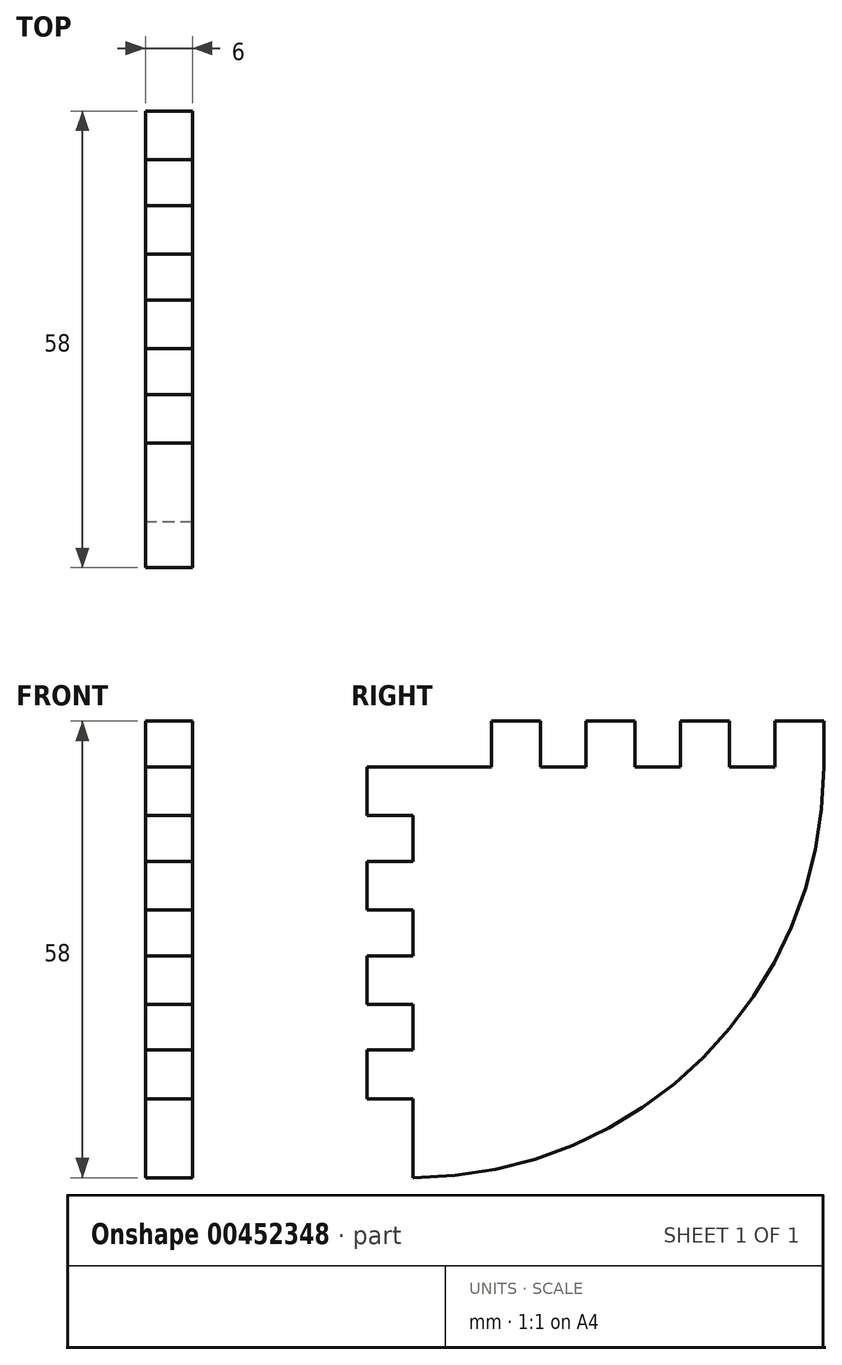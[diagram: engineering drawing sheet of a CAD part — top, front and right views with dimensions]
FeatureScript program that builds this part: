
annotation { "Feature Type Name" : "Feature", "Feature Type Description" : "" }
export const myFeature = defineFeature(function(context is Context, id is Id, definition is map)
    precondition{}
    {
        {
            var Q0;
            Q0=qCreatedBy(makeId("Right.planeOp"),FACE);
            var sketch = newSketch(context, id + "F0", { "sketchPlane" : qUnion([Q0])});
            skLineSegment(sketch, "E0", {"start": v(5.8, -52.2) * mm, "end": v(5.8, -42.2) * mm});
            skLineSegment(sketch, "E1", {"start": v(5.8, -42.2) * mm, "end": v(0, -42.2) * mm});
            skLineSegment(sketch, "E2", {"start": v(0, -42.2) * mm, "end": v(0, -36) * mm});
            skLineSegment(sketch, "E3", {"start": v(0, -36) * mm, "end": v(5.8, -36) * mm});
            skLineSegment(sketch, "E4", {"start": v(5.8, -36) * mm, "end": v(5.8, -30.2) * mm});
            skLineSegment(sketch, "E5", {"start": v(5.8, -30.2) * mm, "end": v(0, -30.2) * mm});
            skLineSegment(sketch, "E6", {"start": v(0, -30.2) * mm, "end": v(0, -24) * mm});
            skLineSegment(sketch, "E7", {"start": v(0, -24) * mm, "end": v(5.8, -24) * mm});
            skLineSegment(sketch, "E8", {"start": v(5.8, -24) * mm, "end": v(5.8, -18.2) * mm});
            skLineSegment(sketch, "E9", {"start": v(5.8, -18.2) * mm, "end": v(0, -18.2) * mm});
            skLineSegment(sketch, "E10", {"start": v(0, -18.2) * mm, "end": v(0, -12) * mm});
            skLineSegment(sketch, "E11", {"start": v(0, -12) * mm, "end": v(5.8, -12) * mm});
            skLineSegment(sketch, "E12", {"start": v(5.8, -12) * mm, "end": v(5.8, -6.2) * mm});
            skLineSegment(sketch, "E13", {"start": v(5.8, -6.2) * mm, "end": v(0, -6.2) * mm});
            skLineSegment(sketch, "E14", {"start": v(0, -6.2) * mm, "end": v(0, 0) * mm});
            skArc(sketch, "E15", {"start": v(58, 0) * mm, "mid": v(42.71, -36.91) * mm, "end": v(5.8, -52.2) * mm});
            skLineSegment(sketch, "E16", {"start": v(58, 0) * mm, "end": v(58, 5.8) * mm});
            skLineSegment(sketch, "E17", {"start": v(58, 5.8) * mm, "end": v(51.8, 5.8) * mm});
            skLineSegment(sketch, "E18", {"start": v(51.8, 5.8) * mm, "end": v(51.8, 0) * mm});
            skLineSegment(sketch, "E19", {"start": v(51.8, 0) * mm, "end": v(46, 0) * mm});
            skLineSegment(sketch, "E20", {"start": v(46, 0) * mm, "end": v(46, 5.8) * mm});
            skLineSegment(sketch, "E21", {"start": v(46, 5.8) * mm, "end": v(39.8, 5.8) * mm});
            skLineSegment(sketch, "E22", {"start": v(39.8, 5.8) * mm, "end": v(39.8, 0) * mm});
            skLineSegment(sketch, "E23", {"start": v(39.8, 0) * mm, "end": v(34, 0) * mm});
            skLineSegment(sketch, "E24", {"start": v(34, 0) * mm, "end": v(34, 5.8) * mm});
            skLineSegment(sketch, "E25", {"start": v(34, 5.8) * mm, "end": v(27.8, 5.8) * mm});
            skLineSegment(sketch, "E26", {"start": v(27.8, 5.8) * mm, "end": v(27.8, 0) * mm});
            skLineSegment(sketch, "E27", {"start": v(27.8, 0) * mm, "end": v(22, 0) * mm});
            skLineSegment(sketch, "E28", {"start": v(22, 0) * mm, "end": v(22, 5.8) * mm});
            skLineSegment(sketch, "E29", {"start": v(22, 5.8) * mm, "end": v(15.8, 5.8) * mm});
            skLineSegment(sketch, "E30", {"start": v(15.8, 5.8) * mm, "end": v(15.8, 0) * mm});
            skLineSegment(sketch, "E31", {"start": v(15.8, 0) * mm, "end": v(0, 0) * mm});
            skSolve(sketch);
        }
        {
            var Q0;
            Q0 = qSketchRegion(id + "F0", true);
            extrude(context, id + "F1", {"entities" : qUnion([Q0]), "depth" : 6 * mm});
        }
    });
